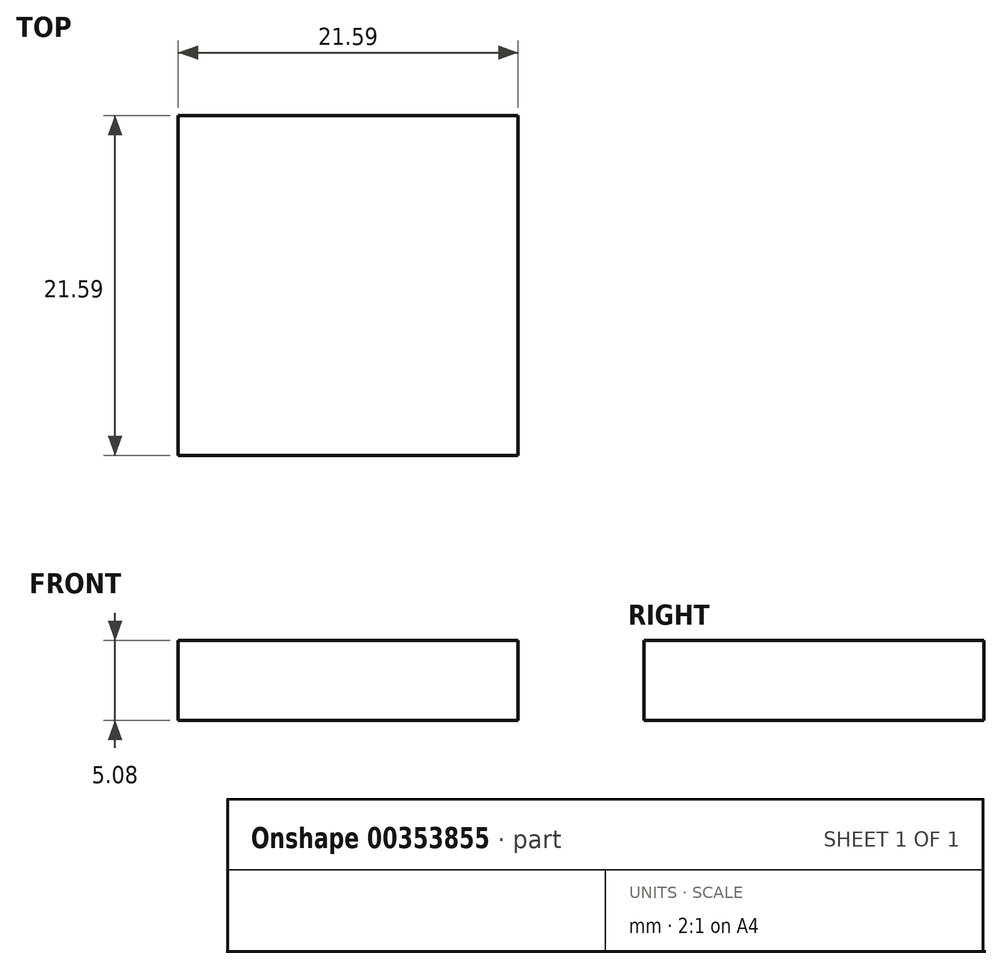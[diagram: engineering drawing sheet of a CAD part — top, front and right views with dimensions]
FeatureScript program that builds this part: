
annotation { "Feature Type Name" : "Feature", "Feature Type Description" : "" }
export const myFeature = defineFeature(function(context is Context, id is Id, definition is map)
    precondition{}
    {
        {
            var Q0;
            Q0=qCreatedBy(makeId("Top.planeOp"),FACE);
            var sketch = newSketch(context, id + "F0", { "sketchPlane" : qUnion([Q0])});
            skLineSegment(sketch, "E0.bottom", {"start": v(0, 0) * mm, "end": v(21.59, 0) * mm});
            skLineSegment(sketch, "E0.top", {"start": v(0, -21.59) * mm, "end": v(21.59, -21.59) * mm});
            skLineSegment(sketch, "E0.left", {"start": v(0, 0) * mm, "end": v(0, -21.59) * mm});
            skLineSegment(sketch, "E0.right", {"start": v(21.59, 0) * mm, "end": v(21.59, -21.59) * mm});
            skSolve(sketch);
        }
        {
            var Q0;
            Q0=makeQuery(id+"F0.imprint","IMPRINT",FACE,{"disambiguationData":[TD([[makeQuery(id+"F0.imprint","IMPRINT",EDGE,{"derivedFrom":sQuery(id+"F0.wireOp",EDGE,"E0.bottom")}),-1.0]])]});
            extrude(context, id + "F1", {"entities" : qUnion([Q0]), "depth" : 5.08 * mm});
        }
    });
